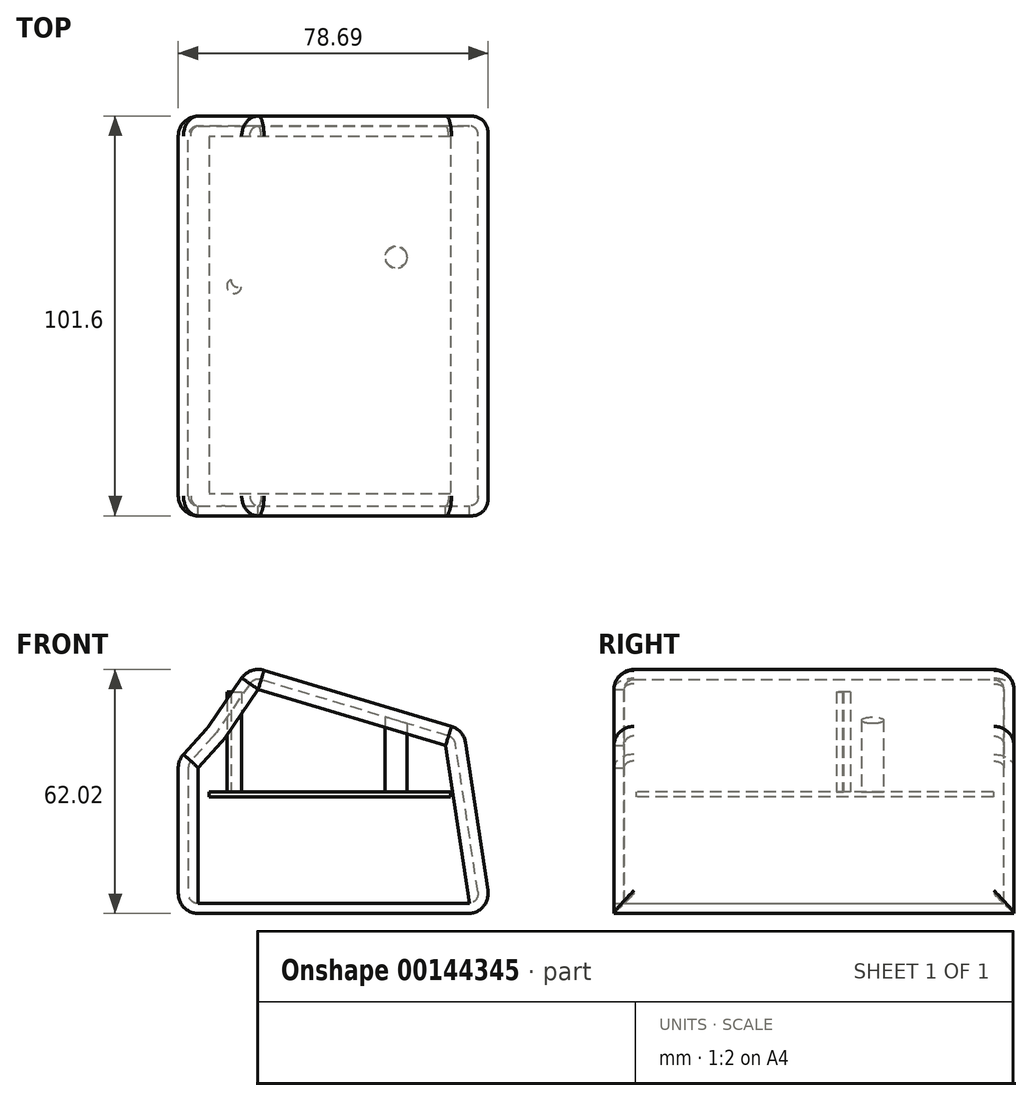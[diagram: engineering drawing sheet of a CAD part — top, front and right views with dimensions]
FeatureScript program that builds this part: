
annotation { "Feature Type Name" : "Feature", "Feature Type Description" : "" }
export const myFeature = defineFeature(function(context is Context, id is Id, definition is map)
    precondition{}
    {
        {
            var Q0;
            Q0=qCreatedBy(makeId("Front.planeOp"),FACE);
            var sketch = newSketch(context, id + "F0", { "sketchPlane" : qUnion([Q0])});
            skLineSegment(sketch, "E0", {"start": v(-28.99, 17.53) * mm, "end": v(-36.43, 9.3) * mm});
            skLineSegment(sketch, "E1", {"start": v(-36.43, 9.3) * mm, "end": v(-36.43, -29.67) * mm});
            skLineSegment(sketch, "E2", {"start": v(-36.43, -29.67) * mm, "end": v(43.09, -29.67) * mm});
            skLineSegment(sketch, "E3", {"start": v(43.09, -29.67) * mm, "end": v(36.04, 16.94) * mm});
            skLineSegment(sketch, "E4", {"start": v(36.04, 16.94) * mm, "end": v(-18.22, 33.2) * mm});
            skLineSegment(sketch, "E5", {"start": v(-18.22, 33.2) * mm, "end": v(-28.99, 17.53) * mm});
            skSolve(sketch);
        }
        {
            var Q0;
            Q0=makeQuery(id+"F0.imprint","IMPRINT",FACE,{"disambiguationData":[TD([[makeQuery(id+"F0.imprint","IMPRINT",EDGE,{"derivedFrom":sQuery(id+"F0.wireOp",EDGE,"E0")}),1.0]])]});
            extrude(context, id + "F1", {"entities" : qUnion([Q0]), "depth" : 101.6 * mm});
        }
        {
            var Q0;
            Q0=makeQuery(id+"F1.opExtrude","SWEPT_FACE",FACE,{"disambiguationData":[OSD([sQuery(id+"F0.wireOp",EDGE,"E4")])]});
            fillet(context, id + "F2", {"entities" : qUnion([Q0]), "radius" : 5.08 * mm, "tangentPropagation" : true, "allowEdgeOverflow" : false});
        }
        {
            var Q0;
            Q0=makeQuery(id+"F1.opExtrude","SWEPT_FACE",FACE,{"disambiguationData":[OSD([sQuery(id+"F0.wireOp",EDGE,"E5")])]});
            fillet(context, id + "F3", {"entities" : qUnion([Q0]), "radius" : 5.08 * mm, "tangentPropagation" : true, "allowEdgeOverflow" : false});
        }
        {
            var Q0;
            Q0=makeQuery(id+"F1.opExtrude","SWEPT_FACE",FACE,{"disambiguationData":[OSD([sQuery(id+"F0.wireOp",EDGE,"E0")])]});
            fillet(context, id + "F4", {"entities" : qUnion([Q0]), "radius" : 5.08 * mm, "tangentPropagation" : true, "allowEdgeOverflow" : false});
        }
        {
            var Q0;
            Q0=makeQuery(id+"F1.opExtrude","SWEPT_FACE",FACE,{"disambiguationData":[OSD([sQuery(id+"F0.wireOp",EDGE,"E3")])]});
            fillet(context, id + "F5", {"entities" : qUnion([Q0]), "radius" : 5.08 * mm, "tangentPropagation" : true, "allowEdgeOverflow" : false});
        }
        {
            var Q0;
            Q0=makeQuery(id+"F1.opExtrude","SWEPT_FACE",FACE,{"disambiguationData":[OSD([sQuery(id+"F0.wireOp",EDGE,"E1")])]});
            fillet(context, id + "F6", {"entities" : qUnion([Q0]), "radius" : 5.08 * mm, "tangentPropagation" : true, "allowEdgeOverflow" : false});
        }
        {
            var Q0;
            Q0=makeQuery(id+"F1.opExtrude","CAP_FACE",FACE,{"disambiguationData":[OSD([sQuery(id+"F0.wireOp",EDGE,"E0"),sQuery(id+"F0.wireOp",EDGE,"E1"),sQuery(id+"F0.wireOp",EDGE,"E2"),sQuery(id+"F0.wireOp",EDGE,"E3"),sQuery(id+"F0.wireOp",EDGE,"E4"),sQuery(id+"F0.wireOp",EDGE,"E5")])],"isStart":false});
            shell(context, id + "F7", {"entities" : qUnion([Q0]), "thickness" : 2.54 * mm});
        }
        {
            var Q0;
            Q0=qCreatedBy(makeId("Top.planeOp"),FACE);
            var sketch = newSketch(context, id + "F8", { "sketchPlane" : qUnion([Q0])});
            skLineSegment(sketch, "E6.bottom", {"start": v(32.68, -5.27) * mm, "end": v(-28.56, -5.27) * mm});
            skLineSegment(sketch, "E6.top", {"start": v(32.68, -96) * mm, "end": v(-28.56, -96) * mm});
            skLineSegment(sketch, "E6.left", {"start": v(32.68, -5.27) * mm, "end": v(32.68, -96) * mm});
            skLineSegment(sketch, "E6.right", {"start": v(-28.56, -5.27) * mm, "end": v(-28.56, -96) * mm});
            skSolve(sketch);
        }
        {
            var Q0;
            Q0=makeQuery(id+"F8.imprint","IMPRINT",FACE,{"disambiguationData":[TD([[makeQuery(id+"F8.imprint","IMPRINT",EDGE,{"derivedFrom":sQuery(id+"F8.wireOp",EDGE,"E6.bottom")}),1.0]])]});
            extrude(context, id + "F9", {"entities" : qUnion([Q0]), "depth" : 1.27 * mm});
        }
        {
            var Q0;
            Q0=makeQuery(id+"F9.opExtrude","CAP_FACE",FACE,{"disambiguationData":[OSD([sQuery(id+"F8.wireOp",EDGE,"E6.bottom"),sQuery(id+"F8.wireOp",EDGE,"E6.top"),sQuery(id+"F8.wireOp",EDGE,"E6.left"),sQuery(id+"F8.wireOp",EDGE,"E6.right")])],"isStart":false});
            var sketch = newSketch(context, id + "F10", { "sketchPlane" : qUnion([Q0])});
            skSolve(sketch);
        }
        {
            var Q0;
            Q0=makeQuery(id+"F10.imprint","IMPRINT",FACE,{"disambiguationData":[TD([[makeQuery(id+"F10.imprint","IMPRINT",EDGE,{"derivedFrom":makeQuery(id+"F9.opExtrude","CAP_EDGE",EDGE,{"disambiguationData":[OSD([sQuery(id+"F8.wireOp",EDGE,"E6.bottom")])],"isStart":false})}),1.0]])]});
            var sketch = newSketch(context, id + "F11", { "sketchPlane" : qUnion([Q0])});
            skCircle(sketch, "E7", {"center": v(-21.2, -41.66) * mm, "radius": 1.85 * mm});
            skCircle(sketch, "E8", {"center": v(-22.22, -43.21) * mm, "radius": 1.85 * mm});
            skSolve(sketch);
        }
        {
            var Q0;
            {var subQ0=sQuery(id+"F11.wireOp",EDGE,"E8");var subQ1=sQuery(id+"F11.wireOp",EDGE,"E7");var subQ2=makeQuery(id+"F11.imprint","INTERSECT",VERTEX,{"disambiguationData":[OD(0.0)],"derivedFrom":[subQ1,subQ0]});Q0=makeQuery(id+"F11.imprint","IMPRINT",FACE,{"disambiguationData":[TD([[makeQuery(id+"F11.imprint","IMPRINT",EDGE,{"disambiguationData":[TD([[subQ2,-1.0]])],"derivedFrom":subQ1}),-1.0]])]});}
            var Q1;
            Q1=sQuery(id+"F11.wireOp",EDGE,"E7");
            extrude(context, id + "F12", {"entities" : qUnion([Q0]), "surfaceEntities" : qUnion([Q1]), "depth" : 25.4 * mm});
        }
        {
            var Q0;
            Q0=makeQuery(id+"F10.imprint","IMPRINT",FACE,{"disambiguationData":[TD([[makeQuery(id+"F10.imprint","IMPRINT",EDGE,{"derivedFrom":makeQuery(id+"F9.opExtrude","CAP_EDGE",EDGE,{"disambiguationData":[OSD([sQuery(id+"F8.wireOp",EDGE,"E6.bottom")])],"isStart":false})}),1.0]])]});
            var sketch = newSketch(context, id + "F13", { "sketchPlane" : qUnion([Q0])});
            skCircle(sketch, "E9", {"center": v(18.93, -35.89) * mm, "radius": 2.8 * mm});
            skSolve(sketch);
        }
        {
            var Q0;
            Q0=makeQuery(id+"F13.imprint","IMPRINT",FACE,{"disambiguationData":[TD([[makeQuery(id+"F13.imprint","IMPRINT",EDGE,{"derivedFrom":sQuery(id+"F13.wireOp",EDGE,"E9")}),1.0]])]});
            var Q1;
            Q1=sQuery(id+"F13.wireOp",EDGE,"E9");
            extrude(context, id + "F14", {"entities" : qUnion([Q0]), "operationType" : NewBodyOperationType.ADD, "surfaceEntities" : qUnion([Q1]), "depth" : 19.05 * mm});
        }
    });
